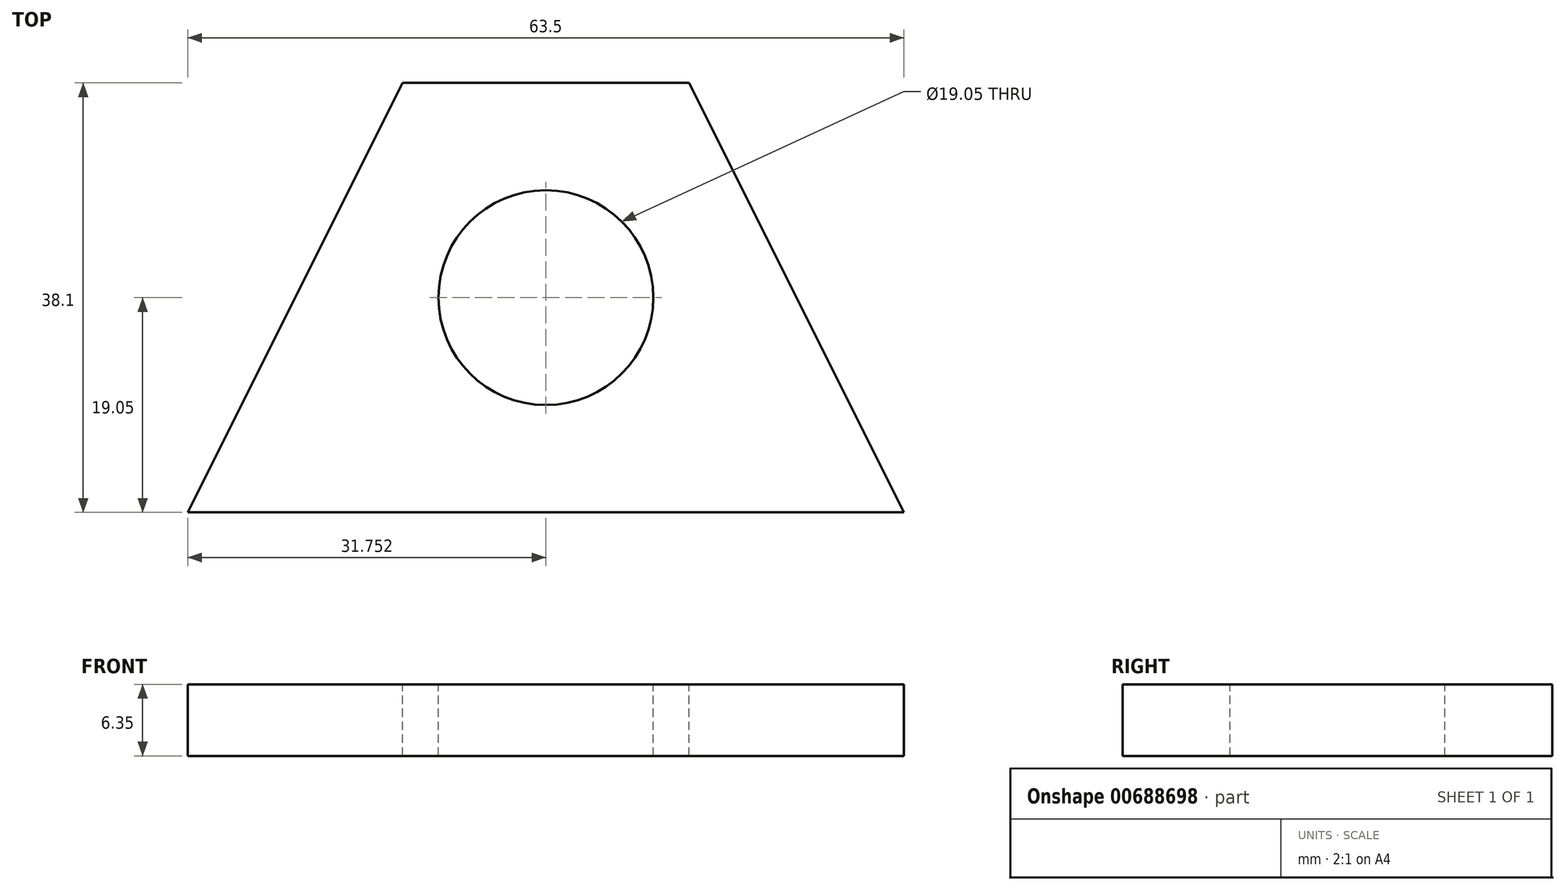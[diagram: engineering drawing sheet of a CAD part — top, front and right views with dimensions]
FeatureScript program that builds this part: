
annotation { "Feature Type Name" : "Feature", "Feature Type Description" : "" }
export const myFeature = defineFeature(function(context is Context, id is Id, definition is map)
    precondition{}
    {
        {
            var Q0;
            Q0=qCreatedBy(makeId("Top.planeOp"),FACE);
            var sketch = newSketch(context, id + "F0", { "sketchPlane" : qUnion([Q0])});
            skLineSegment(sketch, "E0", {"start": v(-29.96, 0) * mm, "end": v(-29.96, 38.1) * mm});
            skLineSegment(sketch, "E1", {"start": v(-29.96, 38.1) * mm, "end": v(33.54, 38.1) * mm});
            skLineSegment(sketch, "E2", {"start": v(33.54, 38.1) * mm, "end": v(33.54, 0) * mm});
            skLineSegment(sketch, "E3", {"start": v(33.54, 0) * mm, "end": v(-29.96, 0) * mm});
            skSolve(sketch);
        }
        {
            var Q0;
            Q0=makeQuery(id+"F0.imprint","IMPRINT",FACE,{"disambiguationData":[TD([[makeQuery(id+"F0.imprint","IMPRINT",EDGE,{"derivedFrom":sQuery(id+"F0.wireOp",EDGE,"E0")}),-1.0]])]});
            extrude(context, id + "F1", {"entities" : qUnion([Q0]), "depth" : 6.35 * mm, "offsetDistance" : 25.4 * mm});
        }
        {
            var Q0;
            Q0=makeQuery(id+"F1.opExtrude","CAP_FACE",FACE,{"disambiguationData":[OSD([sQuery(id+"F0.wireOp",EDGE,"E0"),sQuery(id+"F0.wireOp",EDGE,"E1"),sQuery(id+"F0.wireOp",EDGE,"E2"),sQuery(id+"F0.wireOp",EDGE,"E3")])],"isStart":false});
            var sketch = newSketch(context, id + "F2", { "sketchPlane" : qUnion([Q0])});
            skCircle(sketch, "E4", {"center": v(1.8, 19.05) * mm, "radius": 9.53 * mm});
            skPoint(sketch, "E5.orphan", {"position": v(1.8, 38.1) * mm});
            skPoint(sketch, "E6.orphan", {"position": v(-29.96, 38.1) * mm});
            skPoint(sketch, "E7.trimOffspring.end.orphan", {"position": v(1.8, 0) * mm});
            skPoint(sketch, "E8.end.orphan", {"position": v(33.54, 0) * mm});
            skLineSegment(sketch, "E9", {"start": v(14.5, 38.1) * mm, "end": v(33.54, 0) * mm});
            skLineSegment(sketch, "E10", {"start": v(-10.9, 38.1) * mm, "end": v(-29.96, 0) * mm});
            skSolve(sketch);
        }
        {
            var Q0;
            {var subQ0=sQuery(id+"F2.wireOp",EDGE,"E10");Q0=makeQuery(id+"F2.imprint","IMPRINT",FACE,{"disambiguationData":[TD([[makeQuery(id+"F2.imprint","IMPRINT",EDGE,{"derivedFrom":subQ0}),-1.0]])]});}
            var Q1;
            {var subQ0=sQuery(id+"F2.wireOp",EDGE,"E9");Q1=makeQuery(id+"F2.imprint","IMPRINT",FACE,{"disambiguationData":[TD([[makeQuery(id+"F2.imprint","IMPRINT",EDGE,{"derivedFrom":subQ0}),1.0]])]});}
            var Q2;
            Q2=makeQuery(id+"F2.imprint","IMPRINT",FACE,{"disambiguationData":[TD([[makeQuery(id+"F2.imprint","IMPRINT",EDGE,{"derivedFrom":sQuery(id+"F2.wireOp",EDGE,"E4")}),1.0]])]});
            extrude(context, id + "F3", {"entities" : qUnion([Q0, Q1, Q2]), "operationType" : NewBodyOperationType.REMOVE, "oppositeDirection" : true, "depth" : 25.4 * mm, "offsetDistance" : 25.4 * mm});
        }
    });
